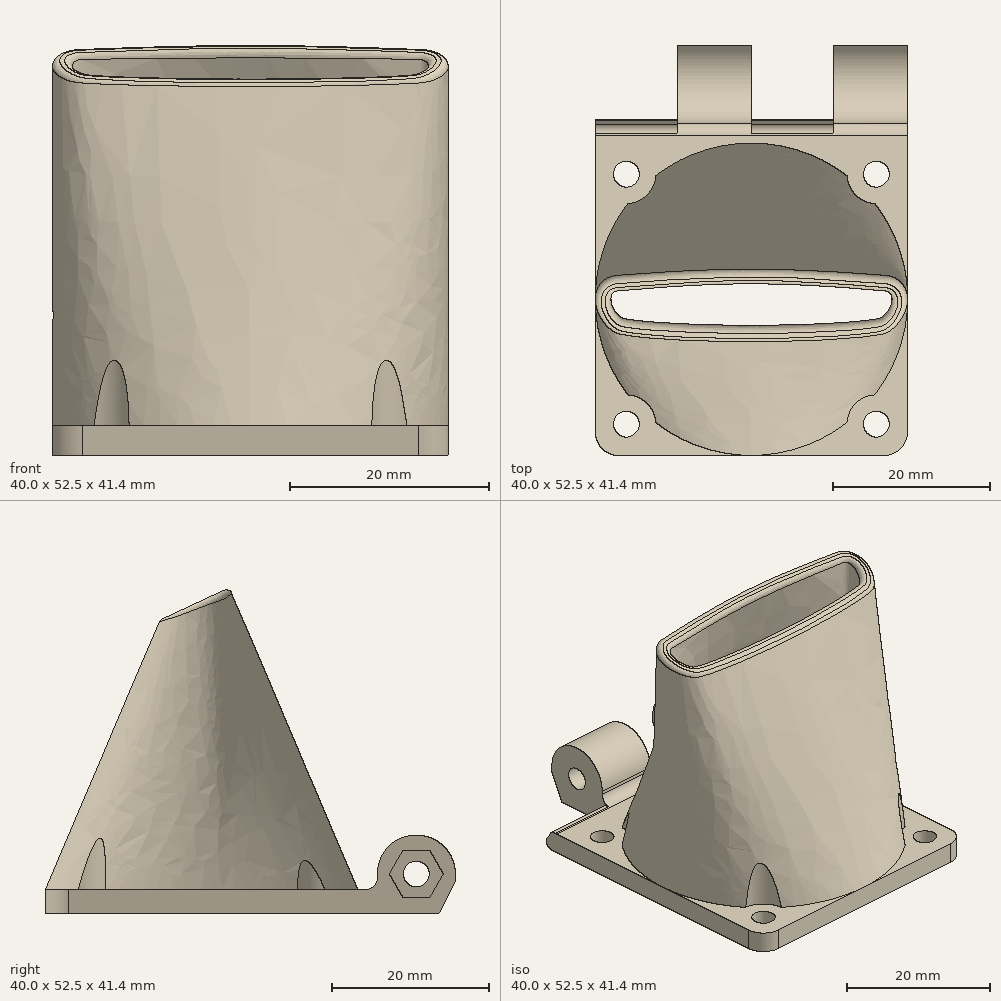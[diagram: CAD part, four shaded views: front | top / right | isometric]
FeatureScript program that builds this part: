
annotation { "Feature Type Name" : "Feature", "Feature Type Description" : "" }
export const myFeature = defineFeature(function(context is Context, id is Id, definition is map)
    precondition{}
    {
        {
            var Q0;
            Q0=qCreatedBy(makeId("Top.planeOp"),FACE);
            var sketch = newSketch(context, id + "F0", { "sketchPlane" : qUnion([Q0])});
            skLineSegment(sketch, "E0.bottom", {"start": v(0, 0) * mm, "end": v(40, 0) * mm, "construction": true});
            skLineSegment(sketch, "E0.top", {"start": v(3, -40) * mm, "end": v(37, -40) * mm});
            skLineSegment(sketch, "E0.left", {"start": v(0, 5) * mm, "end": v(0, -37) * mm});
            skLineSegment(sketch, "E0.right", {"start": v(40, 5) * mm, "end": v(40, -37) * mm});
            skLineSegment(sketch, "E1", {"start": v(0, 0) * mm, "end": v(40, -40) * mm, "construction": true});
            skLineSegment(sketch, "E2", {"start": v(0, -40) * mm, "end": v(40, 0) * mm, "construction": true});
            skLineSegment(sketch, "E3", {"start": v(20, 0) * mm, "end": v(20, -40) * mm, "construction": true});
            skCircle(sketch, "E4", {"center": v(20, -20) * mm, "radius": 18 * mm});
            skCircle(sketch, "E5", {"center": v(4, -4) * mm, "radius": 1.65 * mm});
            skCircle(sketch, "E6", {"center": v(36, -4) * mm, "radius": 1.65 * mm});
            skCircle(sketch, "E7", {"center": v(36, -36) * mm, "radius": 1.65 * mm});
            skCircle(sketch, "E8", {"center": v(4, -36) * mm, "radius": 1.65 * mm});
            skPoint(sketch, "E9.visualSharp", {"position": v(0, -40) * mm});
            skArc(sketch, "E9.filletArc", {"start": v(0, -37) * mm, "mid": v(0.88, -39.12) * mm, "end": v(3, -40) * mm});
            skPoint(sketch, "E10.visualSharp", {"position": v(40, -40) * mm});
            skArc(sketch, "E10.filletArc", {"start": v(37, -40) * mm, "mid": v(39.12, -39.12) * mm, "end": v(40, -37) * mm});
            skPoint(sketch, "E11.visualSharp", {"position": v(40, 0) * mm});
            skPoint(sketch, "E12.visualSharp", {"position": v(0, 0) * mm});
            skLineSegment(sketch, "E13", {"start": v(0, 5) * mm, "end": v(40, 5) * mm});
            skSolve(sketch);
        }
        {
            var Q0;
            Q0 = qSketchRegion(id + "F0", true);
            extrude(context, id + "F1", {"entities" : qUnion([Q0]), "depth" : 3 * mm});
        }
        {
            var Q0;
            Q0=makeQuery(id+"F1.opExtrude","CAP_FACE",FACE,{"disambiguationData":[OSD([sQuery(id+"F0.wireOp",EDGE,"E0.bottom"),sQuery(id+"F0.wireOp",EDGE,"E0.top"),sQuery(id+"F0.wireOp",EDGE,"E0.left"),sQuery(id+"F0.wireOp",EDGE,"E0.right"),sQuery(id+"F0.wireOp",EDGE,"E4"),sQuery(id+"F0.wireOp",EDGE,"E5"),sQuery(id+"F0.wireOp",EDGE,"E6"),sQuery(id+"F0.wireOp",EDGE,"E7"),sQuery(id+"F0.wireOp",EDGE,"E8"),sQuery(id+"F0.wireOp",EDGE,"E9.filletArc"),sQuery(id+"F0.wireOp",EDGE,"E10.filletArc"),sQuery(id+"F0.wireOp",EDGE,"E11.filletArc"),sQuery(id+"F0.wireOp",EDGE,"E12.filletArc")])],"isStart":false});
            var sketch = newSketch(context, id + "F2", { "sketchPlane" : qUnion([Q0])});
            skLineSegment(sketch, "E14", {"start": v(0, 0) * mm, "end": v(20, -20) * mm, "construction": true});
            skLineSegment(sketch, "E15", {"start": v(4, -36) * mm, "end": v(36, -4) * mm, "construction": true});
            skLineSegment(sketch, "E16", {"start": v(20, -20) * mm, "end": v(36, -36) * mm, "construction": true});
            skArc(sketch, "E17", {"start": v(5.86, -5.86) * mm, "mid": v(2.39, -10.53) * mm, "end": v(0.4, -16) * mm});
            skArc(sketch, "E18", {"start": v(5.86, -34.14) * mm, "mid": v(20, -40) * mm, "end": v(34.14, -34.14) * mm});
            skArc(sketch, "E19", {"start": v(34.14, -5.86) * mm, "mid": v(20, 0) * mm, "end": v(5.86, -5.86) * mm});
            skArc(sketch, "E20", {"start": v(34.14, -34.14) * mm, "mid": v(39.15, -25.76) * mm, "end": v(39.6, -16) * mm});
            skLineSegment(sketch, "E21", {"start": v(0, -16) * mm, "end": v(40, -16) * mm, "construction": true});
            skArc(sketch, "E22", {"start": v(0.4, -16) * mm, "mid": v(0.85, -25.76) * mm, "end": v(5.86, -34.14) * mm});
            skArc(sketch, "E23", {"start": v(39.6, -16) * mm, "mid": v(37.61, -10.53) * mm, "end": v(34.14, -5.86) * mm});
            skSolve(sketch);
        }
        {
            var Q0;
            Q0=makeQuery(id+"F2.imprint","IMPRINT",FACE,{"disambiguationData":[TD([[makeQuery(id+"F2.imprint","IMPRINT",EDGE,{"derivedFrom":makeQuery(id+"F1.opExtrude","CAP_EDGE",EDGE,{"disambiguationData":[OSD([sQuery(id+"F0.wireOp",EDGE,"E6")])],"isStart":false})}),-1.0]])]});
            cPlane(context, id + "F3", {"entities" : qUnion([Q0]), "cplaneType" : CPlaneType.OFFSET, "offset" : 40 * mm, "width" : 150 * mm, "height" : 150 * mm});
        }
        {
            var Q0;
            Q0=qCreatedBy(id+"F3.planeOp",FACE);
            var sketch = newSketch(context, id + "F4", { "sketchPlane" : qUnion([Q0])});
            skLineSegment(sketch, "E24", {"start": v(20, -20) * mm, "end": v(40, -20) * mm, "construction": true});
            skArc(sketch, "E25", {"start": v(3, -17) * mm, "mid": v(0.88, -17.88) * mm, "end": v(0, -20) * mm});
            skArc(sketch, "E26", {"start": v(37, -23) * mm, "mid": v(39.12, -22.12) * mm, "end": v(40, -20) * mm});
            skLineSegment(sketch, "E27", {"start": v(3, -17) * mm, "end": v(37, -17) * mm});
            skLineSegment(sketch, "E28", {"start": v(3, -23) * mm, "end": v(37, -23) * mm});
            skLineSegment(sketch, "E29", {"start": v(0, 0) * mm, "end": v(20, -20) * mm, "construction": true});
            skLineSegment(sketch, "E30", {"start": v(0, -20) * mm, "end": v(20, -20) * mm, "construction": true});
            skArc(sketch, "E31", {"start": v(0, -20) * mm, "mid": v(0.88, -22.12) * mm, "end": v(3, -23) * mm});
            skArc(sketch, "E32", {"start": v(40, -20) * mm, "mid": v(39.12, -17.88) * mm, "end": v(37, -17) * mm});
            skSolve(sketch);
        }
        {
            var Q0;
            Q0=makeQuery(id+"F1.opExtrude","SWEPT_FACE",FACE,{"disambiguationData":[OSD([sQuery(id+"F0.wireOp",EDGE,"E0.top")])]});
            cPlane(context, id + "F5", {"entities" : qUnion([Q0]), "cplaneType" : CPlaneType.OFFSET, "offset" : 20 * mm, "oppositeDirection" : true, "width" : 150 * mm, "height" : 150 * mm});
        }
        {
            var Q0;
            Q0=qCreatedBy(id+"F5.planeOp",FACE);
            var sketch = newSketch(context, id + "F6", { "sketchPlane" : qUnion([Q0])});
            skLineSegment(sketch, "E33", {"start": v(0, 0) * mm, "end": v(0, 3) * mm, "construction": true});
            skLineSegment(sketch, "E34", {"start": v(0, 3) * mm, "end": v(0, 43) * mm});
            skLineSegment(sketch, "E35", {"start": v(0, 0) * mm, "end": v(40, 0) * mm, "construction": true});
            skLineSegment(sketch, "E36", {"start": v(40, 0) * mm, "end": v(40, 3) * mm, "construction": true});
            skLineSegment(sketch, "E37", {"start": v(40, 3) * mm, "end": v(40, 43) * mm});
            skSolve(sketch);
        }
        {
            var Q0;
            Q0=makeQuery(id+"F1.opExtrude","SWEPT_FACE",FACE,{"disambiguationData":[OSD([sQuery(id+"F0.wireOp",EDGE,"E0.right")])]});
            cPlane(context, id + "F7", {"entities" : qUnion([Q0]), "cplaneType" : CPlaneType.OFFSET, "offset" : 20 * mm, "oppositeDirection" : true, "width" : 150 * mm, "height" : 150 * mm});
        }
        {
            var Q0;
            Q0=qCreatedBy(id+"F7.planeOp",FACE);
            var sketch = newSketch(context, id + "F8", { "sketchPlane" : qUnion([Q0])});
            skLineSegment(sketch, "E38", {"start": v(0, 0) * mm, "end": v(0, 3) * mm, "construction": true});
            skLineSegment(sketch, "E39", {"start": v(0, 3) * mm, "end": v(-40, 3) * mm, "construction": true});
            skLineSegment(sketch, "E40", {"start": v(0, 3) * mm, "end": v(0, 43) * mm, "construction": true});
            skLineSegment(sketch, "E41", {"start": v(0, 43) * mm, "end": v(-17, 43) * mm, "construction": true});
            skLineSegment(sketch, "E42", {"start": v(-17, 43) * mm, "end": v(-23, 43) * mm, "construction": true});
            skLineSegment(sketch, "E43", {"start": v(-23, 43) * mm, "end": v(-23, 46) * mm, "construction": true});
            skLineSegment(sketch, "E44", {"start": v(-40, 3) * mm, "end": v(-40, 0) * mm, "construction": true});
            skLineSegment(sketch, "E45", {"start": v(-23, 43) * mm, "end": v(-40, 3) * mm});
            skLineSegment(sketch, "E46", {"start": v(-17, 43) * mm, "end": v(0, 3) * mm});
            skSolve(sketch);
        }
        {
            var Q1;
            Q1 = qSketchRegion(id + "F4", true);
            var Q2;
            Q2 = qSketchRegion(id + "F2", true);
            var Q3;
            Q3=sQuery(id+"F6.wireOp",EDGE,"E34");
            var Q4;
            Q4=sQuery(id+"F6.wireOp",EDGE,"E37");
            var Q5;
            Q5=sQuery(id+"F8.wireOp",EDGE,"E46");
            var Q6;
            Q6=sQuery(id+"F8.wireOp",EDGE,"E45");
            loft(context, id + "F9", {"addGuides" : true, "sheetProfilesArray" : [{ "sheetProfileEntities" : qUnion([Q1]) }, { "sheetProfileEntities" : qUnion([Q2]) }], "guidesArray" : [{ "guideEntities" : qUnion([Q3]), "guideDerivativeType" : LoftGuideDerivativeType.DEFAULT, "guideDerivativeMagnitude" : 1 }, { "guideEntities" : qUnion([Q4]), "guideDerivativeType" : LoftGuideDerivativeType.DEFAULT, "guideDerivativeMagnitude" : 1 }, { "guideEntities" : qUnion([Q5]), "guideDerivativeType" : LoftGuideDerivativeType.DEFAULT, "guideDerivativeMagnitude" : 1 }, { "guideEntities" : qUnion([Q6]), "guideDerivativeType" : LoftGuideDerivativeType.DEFAULT, "guideDerivativeMagnitude" : 1 }]});
        }
        {
            var Q0;
            Q0=makeQuery(id+"F9.opLoft","CAP_FACE",FACE,{"disambiguationData":[OSD([makeQuery(id+"F4.imprint","IMPRINT",FACE,{"disambiguationData":[TD([[makeQuery(id+"F4.imprint","IMPRINT",EDGE,{"derivedFrom":sQuery(id+"F4.wireOp",EDGE,"E25")}),1.0]])]})])],"isStart":true});
            var Q1;
            {var subQ7=sQuery(id+"F2.wireOp",EDGE,"E17");Q1=makeQuery(id+"F9.opLoft","CAP_FACE",FACE,{"disambiguationData":[OSD([makeQuery(id+"F2.imprint","IMPRINT",FACE,{"disambiguationData":[TD([[makeQuery(id+"F2.imprint","IMPRINT",EDGE,{"derivedFrom":subQ7}),1.0]])]})])],"isStart":true});}
            shell(context, id + "F10", {"entities" : qUnion([Q0, Q1]), "thickness" : 2 * mm});
        }
        {
            var Q0;
            Q0=makeQuery(id+"F1.opExtrude","SWEPT_BODY",BODY,{"disambiguationData":[OSD([sQuery(id+"F0.wireOp",EDGE,"E0.bottom"),sQuery(id+"F0.wireOp",EDGE,"E0.top"),sQuery(id+"F0.wireOp",EDGE,"E0.left"),sQuery(id+"F0.wireOp",EDGE,"E0.right"),sQuery(id+"F0.wireOp",EDGE,"E4"),sQuery(id+"F0.wireOp",EDGE,"E5"),sQuery(id+"F0.wireOp",EDGE,"E6"),sQuery(id+"F0.wireOp",EDGE,"E7"),sQuery(id+"F0.wireOp",EDGE,"E8"),sQuery(id+"F0.wireOp",EDGE,"E9.filletArc"),sQuery(id+"F0.wireOp",EDGE,"E10.filletArc"),sQuery(id+"F0.wireOp",EDGE,"E11.filletArc"),sQuery(id+"F0.wireOp",EDGE,"E12.filletArc")])]});
            var Q1;
            Q1=makeQuery(id+"F9.opLoft","SWEPT_BODY",BODY,{"disambiguationData":[OSD([makeQuery(id+"F2.imprint","IMPRINT",FACE,{"disambiguationData":[TD([[makeQuery(id+"F2.imprint","IMPRINT",EDGE,{"derivedFrom":makeQuery(id+"F1.opExtrude","CAP_EDGE",EDGE,{"disambiguationData":[OSD([sQuery(id+"F0.wireOp",EDGE,"E4")])],"isStart":false})}),1.0]])]}),makeQuery(id+"F4.imprint","IMPRINT",FACE,{"disambiguationData":[TD([[makeQuery(id+"F4.imprint","IMPRINT",EDGE,{"derivedFrom":sQuery(id+"F4.wireOp",EDGE,"E25")}),1.0]])]}),sQuery(id+"F6.wireOp",EDGE,"E34"),sQuery(id+"F6.wireOp",EDGE,"E37")])]});
            booleanBodies(context, id + "F11", {"operationType" : BooleanOperationType.UNION, "tools" : qUnion([Q0, Q1])});
        }
        {
            var Q0;
            Q0=qCreatedBy(makeId("Right.planeOp"),FACE);
            var sketch = newSketch(context, id + "F12", { "sketchPlane" : qUnion([Q0])});
            skLineSegment(sketch, "E47", {"start": v(0, 0) * mm, "end": v(-20, 0) * mm, "construction": true});
            skLineSegment(sketch, "E48", {"start": v(-20, 0) * mm, "end": v(-20, 40) * mm, "construction": true});
            skLineSegment(sketch, "E49", {"start": v(-20, 40) * mm, "end": v(-1.87, 48.45) * mm});
            skLineSegment(sketch, "E50", {"start": v(-1.87, 48.45) * mm, "end": v(-6.95, 59.33) * mm});
            skLineSegment(sketch, "E51", {"start": v(-6.95, 59.33) * mm, "end": v(-43.2, 42.42) * mm});
            skLineSegment(sketch, "E52", {"start": v(-43.2, 42.42) * mm, "end": v(-38.13, 31.55) * mm});
            skLineSegment(sketch, "E53", {"start": v(-38.13, 31.55) * mm, "end": v(-20, 40) * mm});
            skSolve(sketch);
        }
        {
            var Q0;
            Q0 = qSketchRegion(id + "F12", true);
            extrude(context, id + "F13", {"entities" : qUnion([Q0]), "operationType" : NewBodyOperationType.REMOVE, "endBound" : BoundingType.THROUGH_ALL, "depth" : 25 * mm});
        }
        {
            var Q0;
            Q0=makeQuery(id+"F13.boolean.opBoolean","INTERSECT",EDGE,{"derivedFrom":[makeQuery(id+"F10.opShell","OFFSET_FACE",FACE,{"disambiguationData":[OSD([sQuery(id+"F2.wireOp",EDGE,"E17"),sQuery(id+"F2.wireOp",EDGE,"E18"),sQuery(id+"F2.wireOp",EDGE,"E22"),sQuery(id+"F4.wireOp",EDGE,"E31"),sQuery(id+"F6.wireOp",EDGE,"E34")])]}),makeQuery(id+"F13.opExtrude","SWEPT_FACE",FACE,{"disambiguationData":[OSD([sQuery(id+"F12.wireOp",EDGE,"E49"),sQuery(id+"F12.wireOp",EDGE,"E53")])]})]});
            var Q1;
            Q1=makeQuery(id+"F13.boolean.opBoolean","INTERSECT",EDGE,{"derivedFrom":[makeQuery(id+"F9.opLoft","SWEPT_FACE",FACE,{"disambiguationData":[OSD([sQuery(id+"F2.wireOp",EDGE,"E17"),sQuery(id+"F2.wireOp",EDGE,"E18"),sQuery(id+"F2.wireOp",EDGE,"E22"),sQuery(id+"F4.wireOp",EDGE,"E31"),sQuery(id+"F6.wireOp",EDGE,"E34")])]}),makeQuery(id+"F13.opExtrude","SWEPT_FACE",FACE,{"disambiguationData":[OSD([sQuery(id+"F12.wireOp",EDGE,"E49"),sQuery(id+"F12.wireOp",EDGE,"E53")])]})]});
            fillet(context, id + "F14", {"entities" : qUnion([Q0, Q1]), "radius" : 0.75 * mm, "tangentPropagation" : true, "allowEdgeOverflow" : false});
        }
        {
            var Q0;
            {var subQ0=sQuery(id+"F0.wireOp",EDGE,"E0.right");var subQ1=sQuery(id+"F0.wireOp",EDGE,"E10.filletArc");var subQ2=sQuery(id+"F0.wireOp",EDGE,"E7");var subQ3=sQuery(id+"F0.wireOp",EDGE,"E0.top");var subQ4=makeQuery(id+"F1.opExtrude","CAP_FACE",FACE,{"disambiguationData":[OSD([sQuery(id+"F0.wireOp",EDGE,"E0.bottom"),subQ3,sQuery(id+"F0.wireOp",EDGE,"E0.left"),subQ0,sQuery(id+"F0.wireOp",EDGE,"E4"),sQuery(id+"F0.wireOp",EDGE,"E5"),sQuery(id+"F0.wireOp",EDGE,"E6"),subQ2,sQuery(id+"F0.wireOp",EDGE,"E8"),sQuery(id+"F0.wireOp",EDGE,"E9.filletArc"),subQ1,sQuery(id+"F0.wireOp",EDGE,"E11.filletArc"),sQuery(id+"F0.wireOp",EDGE,"E12.filletArc")])],"isStart":false});Q0=makeQuery(id+"F11.opBoolean","SPLIT",FACE,{"disambiguationData":[TD([makeQuery(id+"F1.opExtrude","SWEPT_FACE",FACE,{"disambiguationData":[OSD([subQ2])]})])],"derivedFrom":subQ4});}
            var sketch = newSketch(context, id + "F15", { "sketchPlane" : qUnion([Q0])});
            skCircle(sketch, "E54", {"center": v(36, -36) * mm, "radius": 3.75 * mm});
            skLineSegment(sketch, "E55.bottom", {"start": v(36, -36) * mm, "end": v(4, -36) * mm, "construction": true});
            skLineSegment(sketch, "E55.top", {"start": v(36, -4) * mm, "end": v(4, -4) * mm, "construction": true});
            skLineSegment(sketch, "E55.left", {"start": v(36, -36) * mm, "end": v(36, -4) * mm, "construction": true});
            skLineSegment(sketch, "E55.right", {"start": v(4, -36) * mm, "end": v(4, -4) * mm, "construction": true});
            skCircle(sketch, "E56", {"center": v(4, -36) * mm, "radius": 3.75 * mm});
            skCircle(sketch, "E57", {"center": v(4, -4) * mm, "radius": 3.75 * mm});
            skCircle(sketch, "E58", {"center": v(36, -4) * mm, "radius": 3.75 * mm});
            skSolve(sketch);
        }
        {
            var Q0;
            Q0 = qSketchRegion(id + "F15", true);
            extrude(context, id + "F16", {"entities" : qUnion([Q0]), "operationType" : NewBodyOperationType.REMOVE, "depth" : 25 * mm});
        }
        {
            var Q0;
            Q0=qCreatedBy(makeId("Right.planeOp"),FACE);
            var sketch = newSketch(context, id + "F17", { "sketchPlane" : qUnion([Q0])});
            skLineSegment(sketch, "E59.bottom", {"start": v(2.5, 0) * mm, "end": v(10.5, 0) * mm});
            skLineSegment(sketch, "E59.top", {"start": v(2.5, 5) * mm, "end": v(12.5, 5) * mm, "construction": true});
            skLineSegment(sketch, "E59.left", {"start": v(2.5, 0) * mm, "end": v(2.5, 5) * mm});
            skLineSegment(sketch, "E59.right", {"start": v(12.5, 4) * mm, "end": v(12.5, 5) * mm});
            skArc(sketch, "E60", {"start": v(12.5, 5) * mm, "mid": v(7.5, 10) * mm, "end": v(2.5, 5) * mm});
            skLineSegment(sketch, "E61", {"start": v(7.5, 5) * mm, "end": v(7.5, 0) * mm, "construction": true});
            skCircle(sketch, "E62", {"center": v(7.5, 5) * mm, "radius": 1.65 * mm});
            skLineSegment(sketch, "E63", {"start": v(10.5, 0) * mm, "end": v(12.5, 4) * mm});
            skPoint(sketch, "E64.orphan", {"position": v(12.5, 0) * mm});
            skSolve(sketch);
        }
        {
            var Q0;
            Q0 = qSketchRegion(id + "F17", true);
            extrude(context, id + "F18", {"entities" : qUnion([Q0]), "operationType" : NewBodyOperationType.ADD, "depth" : 40 * mm});
        }
        {
            var Q0;
            Q0=makeQuery(id+"F18.boolean.opBoolean","MERGE",FACE,{"derivedFrom":[makeQuery(id+"F1.opExtrude","SWEPT_FACE",FACE,{"disambiguationData":[OSD([sQuery(id+"F0.wireOp",EDGE,"E0.right")])]}),makeQuery(id+"F18.opExtrude","CAP_FACE",FACE,{"disambiguationData":[OSD([sQuery(id+"F17.wireOp",EDGE,"E59.bottom"),sQuery(id+"F17.wireOp",EDGE,"E59.left"),sQuery(id+"F17.wireOp",EDGE,"E59.right"),sQuery(id+"F17.wireOp",EDGE,"E60"),sQuery(id+"F17.wireOp",EDGE,"E62"),sQuery(id+"F17.wireOp",EDGE,"E63")])],"isStart":false})]});
            cPlane(context, id + "F19", {"entities" : qUnion([Q0]), "cplaneType" : CPlaneType.OFFSET, "offset" : 9.5 * mm, "oppositeDirection" : true, "width" : 150 * mm, "height" : 150 * mm});
        }
        {
            var Q0;
            Q0=qCreatedBy(id+"F19.planeOp",FACE);
            var sketch = newSketch(context, id + "F20", { "sketchPlane" : qUnion([Q0])});
            skLineSegment(sketch, "E65", {"start": v(0, 0) * mm, "end": v(7.5, 0) * mm, "construction": true});
            skLineSegment(sketch, "E66", {"start": v(7.5, 0) * mm, "end": v(7.5, 5) * mm, "construction": true});
            skArc(sketch, "E67", {"start": v(13.25, 5) * mm, "mid": v(3.43, 9.07) * mm, "end": v(7.5, -0.75) * mm});
            skLineSegment(sketch, "E68", {"start": v(7.5, -0.75) * mm, "end": v(13.25, -0.75) * mm});
            skLineSegment(sketch, "E69", {"start": v(13.25, 5) * mm, "end": v(13.25, -0.75) * mm});
            skSolve(sketch);
        }
        {
            var Q0;
            Q0 = qSketchRegion(id + "F20", true);
            extrude(context, id + "F21", {"entities" : qUnion([Q0]), "operationType" : NewBodyOperationType.REMOVE, "oppositeDirection" : true, "depth" : 10.5 * mm});
        }
        {
            var Q0;
            Q0=makeQuery(id+"F18.boolean.opBoolean","MERGE",FACE,{"derivedFrom":[makeQuery(id+"F1.opExtrude","SWEPT_FACE",FACE,{"disambiguationData":[OSD([sQuery(id+"F0.wireOp",EDGE,"E0.right")])]}),makeQuery(id+"F18.opExtrude","CAP_FACE",FACE,{"disambiguationData":[OSD([sQuery(id+"F17.wireOp",EDGE,"E59.bottom"),sQuery(id+"F17.wireOp",EDGE,"E59.left"),sQuery(id+"F17.wireOp",EDGE,"E59.right"),sQuery(id+"F17.wireOp",EDGE,"E60"),sQuery(id+"F17.wireOp",EDGE,"E62"),sQuery(id+"F17.wireOp",EDGE,"E63")])],"isStart":false})]});
            cPlane(context, id + "F22", {"entities" : qUnion([Q0]), "cplaneType" : CPlaneType.OFFSET, "offset" : 29.5 * mm, "oppositeDirection" : true, "width" : 150 * mm, "height" : 150 * mm});
        }
        {
            var Q0;
            Q0=qCreatedBy(id+"F22.planeOp",FACE);
            var sketch = newSketch(context, id + "F23", { "sketchPlane" : qUnion([Q0])});
            skLineSegment(sketch, "E70", {"start": v(0, 0) * mm, "end": v(7.5, 0) * mm, "construction": true});
            skLineSegment(sketch, "E71", {"start": v(7.5, 0) * mm, "end": v(7.5, 5) * mm, "construction": true});
            skArc(sketch, "E72", {"start": v(13.25, 5) * mm, "mid": v(3.43, 9.07) * mm, "end": v(7.5, -0.75) * mm});
            skLineSegment(sketch, "E73", {"start": v(7.5, -0.75) * mm, "end": v(13.25, -0.75) * mm});
            skLineSegment(sketch, "E74", {"start": v(13.25, 5) * mm, "end": v(13.25, -0.75) * mm});
            skSolve(sketch);
        }
        {
            var Q0;
            Q0 = qSketchRegion(id + "F23", true);
            extrude(context, id + "F24", {"entities" : qUnion([Q0]), "operationType" : NewBodyOperationType.REMOVE, "endBound" : BoundingType.THROUGH_ALL, "oppositeDirection" : true, "depth" : 25 * mm});
        }
        {
            var Q0;
            {var subQ0=makeQuery(id+"F16.opExtrude","CAP_FACE",FACE,{"disambiguationData":[OSD([sQuery(id+"F15.wireOp",EDGE,"E58")])],"isStart":true});var subQ1=sQuery(id+"F0.wireOp",EDGE,"E13");var subQ2=sQuery(id+"F0.wireOp",EDGE,"E6");var subQ3=sQuery(id+"F0.wireOp",EDGE,"E5");var subQ4=sQuery(id+"F0.wireOp",EDGE,"E0.right");var subQ5=sQuery(id+"F0.wireOp",EDGE,"E0.left");var subQ6=makeQuery(id+"F1.opExtrude","CAP_FACE",FACE,{"disambiguationData":[OSD([sQuery(id+"F0.wireOp",EDGE,"E0.top"),subQ5,subQ4,sQuery(id+"F0.wireOp",EDGE,"E4"),subQ3,subQ2,sQuery(id+"F0.wireOp",EDGE,"E7"),sQuery(id+"F0.wireOp",EDGE,"E8"),sQuery(id+"F0.wireOp",EDGE,"E9.filletArc"),sQuery(id+"F0.wireOp",EDGE,"E10.filletArc"),subQ1])],"isStart":false});var subQ7=makeQuery(id+"F1.opExtrude","SWEPT_FACE",FACE,{"disambiguationData":[OSD([subQ4])]});var subQ8=makeQuery(id+"F16.opExtrude","CAP_FACE",FACE,{"disambiguationData":[OSD([sQuery(id+"F15.wireOp",EDGE,"E57")])],"isStart":true});var subQ9=sQuery(id+"F17.wireOp",EDGE,"E59.left");var subQ10=makeQuery(id+"F18.opExtrude","SWEPT_FACE",FACE,{"disambiguationData":[OSD([subQ9])]});Q0=makeQuery(id+"F21.boolean.opBoolean","SPLIT",EDGE,{"disambiguationData":[TD([subQ7])],"derivedFrom":makeQuery(id+"F18.boolean.opBoolean","INTERSECT",EDGE,{"derivedFrom":[makeQuery(id+"F16.boolean.opBoolean","MERGE",FACE,{"derivedFrom":[makeQuery(id+"F11.opBoolean","SPLIT",FACE,{"disambiguationData":[TD([makeQuery(id+"F1.opExtrude","SWEPT_FACE",FACE,{"disambiguationData":[OSD([subQ3])]})])],"derivedFrom":subQ6}),subQ8,subQ0]}),subQ10]})});}
            fillet(context, id + "F25", {"entities" : qUnion([Q0]), "radius" : 1.5 * mm, "allowEdgeOverflow" : false});
        }
        {
            var Q0;
            {var subQ0=makeQuery(id+"F16.opExtrude","CAP_FACE",FACE,{"disambiguationData":[OSD([sQuery(id+"F15.wireOp",EDGE,"E58")])],"isStart":true});var subQ1=sQuery(id+"F0.wireOp",EDGE,"E13");var subQ2=sQuery(id+"F0.wireOp",EDGE,"E6");var subQ3=sQuery(id+"F0.wireOp",EDGE,"E5");var subQ4=sQuery(id+"F0.wireOp",EDGE,"E0.right");var subQ5=sQuery(id+"F0.wireOp",EDGE,"E0.left");var subQ6=makeQuery(id+"F1.opExtrude","CAP_FACE",FACE,{"disambiguationData":[OSD([sQuery(id+"F0.wireOp",EDGE,"E0.top"),subQ5,subQ4,sQuery(id+"F0.wireOp",EDGE,"E4"),subQ3,subQ2,sQuery(id+"F0.wireOp",EDGE,"E7"),sQuery(id+"F0.wireOp",EDGE,"E8"),sQuery(id+"F0.wireOp",EDGE,"E9.filletArc"),sQuery(id+"F0.wireOp",EDGE,"E10.filletArc"),subQ1])],"isStart":false});var subQ7=makeQuery(id+"F1.opExtrude","SWEPT_FACE",FACE,{"disambiguationData":[OSD([subQ4])]});var subQ8=makeQuery(id+"F16.opExtrude","CAP_FACE",FACE,{"disambiguationData":[OSD([sQuery(id+"F15.wireOp",EDGE,"E57")])],"isStart":true});var subQ9=sQuery(id+"F17.wireOp",EDGE,"E59.left");var subQ10=makeQuery(id+"F18.opExtrude","SWEPT_FACE",FACE,{"disambiguationData":[OSD([subQ9])]});Q0=makeQuery(id+"F25.opFillet","BLEND_EDGE",EDGE,{"blendedFrom":[makeQuery(id+"F21.boolean.opBoolean","SPLIT",EDGE,{"disambiguationData":[TD([subQ7])],"derivedFrom":makeQuery(id+"F18.boolean.opBoolean","INTERSECT",EDGE,{"derivedFrom":[makeQuery(id+"F16.boolean.opBoolean","MERGE",FACE,{"derivedFrom":[makeQuery(id+"F11.opBoolean","SPLIT",FACE,{"disambiguationData":[TD([makeQuery(id+"F1.opExtrude","SWEPT_FACE",FACE,{"disambiguationData":[OSD([subQ3])]})])],"derivedFrom":subQ6}),subQ8,subQ0]}),subQ10]})}),makeQuery(id+"F24.boolean.opBoolean","COPY",FACE,{"derivedFrom":makeQuery(id+"F24.opExtrude","SWEPT_FACE",FACE,{"disambiguationData":[OSD([sQuery(id+"F23.wireOp",EDGE,"E72")])]})})],"blendedInto":[makeQuery(id+"F24.boolean.opBoolean","COPY",FACE,{"derivedFrom":makeQuery(id+"F24.opExtrude","SWEPT_FACE",FACE,{"disambiguationData":[OSD([sQuery(id+"F23.wireOp",EDGE,"E72")])]})})]});}
            var Q1;
            {var subQ0=sQuery(id+"F20.wireOp",EDGE,"E67");var subQ1=makeQuery(id+"F16.opExtrude","CAP_FACE",FACE,{"disambiguationData":[OSD([sQuery(id+"F15.wireOp",EDGE,"E58")])],"isStart":true});var subQ2=sQuery(id+"F0.wireOp",EDGE,"E13");var subQ3=sQuery(id+"F0.wireOp",EDGE,"E6");var subQ4=sQuery(id+"F0.wireOp",EDGE,"E5");var subQ5=sQuery(id+"F0.wireOp",EDGE,"E0.right");var subQ6=sQuery(id+"F0.wireOp",EDGE,"E0.left");var subQ7=makeQuery(id+"F1.opExtrude","CAP_FACE",FACE,{"disambiguationData":[OSD([sQuery(id+"F0.wireOp",EDGE,"E0.top"),subQ6,subQ5,sQuery(id+"F0.wireOp",EDGE,"E4"),subQ4,subQ3,sQuery(id+"F0.wireOp",EDGE,"E7"),sQuery(id+"F0.wireOp",EDGE,"E8"),sQuery(id+"F0.wireOp",EDGE,"E9.filletArc"),sQuery(id+"F0.wireOp",EDGE,"E10.filletArc"),subQ2])],"isStart":false});var subQ8=makeQuery(id+"F1.opExtrude","SWEPT_FACE",FACE,{"disambiguationData":[OSD([subQ5])]});var subQ9=makeQuery(id+"F16.opExtrude","CAP_FACE",FACE,{"disambiguationData":[OSD([sQuery(id+"F15.wireOp",EDGE,"E57")])],"isStart":true});var subQ10=sQuery(id+"F17.wireOp",EDGE,"E59.left");var subQ11=makeQuery(id+"F18.opExtrude","SWEPT_FACE",FACE,{"disambiguationData":[OSD([subQ10])]});Q1=makeQuery(id+"F25.opFillet","BLEND_EDGE",EDGE,{"blendedFrom":[makeQuery(id+"F21.boolean.opBoolean","SPLIT",EDGE,{"disambiguationData":[TD([subQ8])],"derivedFrom":makeQuery(id+"F18.boolean.opBoolean","INTERSECT",EDGE,{"derivedFrom":[makeQuery(id+"F16.boolean.opBoolean","MERGE",FACE,{"derivedFrom":[makeQuery(id+"F11.opBoolean","SPLIT",FACE,{"disambiguationData":[TD([makeQuery(id+"F1.opExtrude","SWEPT_FACE",FACE,{"disambiguationData":[OSD([subQ4])]})])],"derivedFrom":subQ7}),subQ9,subQ1]}),subQ11]})}),makeQuery(id+"F21.boolean.opBoolean","COPY",FACE,{"derivedFrom":makeQuery(id+"F21.opExtrude","SWEPT_FACE",FACE,{"disambiguationData":[OSD([subQ0])]})})],"blendedInto":[makeQuery(id+"F21.boolean.opBoolean","COPY",FACE,{"derivedFrom":makeQuery(id+"F21.opExtrude","SWEPT_FACE",FACE,{"disambiguationData":[OSD([subQ0])]})})]});}
            var Q2;
            Q2=makeQuery(id+"F24.boolean.opBoolean","INTERSECT",EDGE,{"derivedFrom":[makeQuery(id+"F18.boolean.opBoolean","MERGE",FACE,{"derivedFrom":[makeQuery(id+"F1.opExtrude","CAP_FACE",FACE,{"disambiguationData":[OSD([sQuery(id+"F0.wireOp",EDGE,"E0.top"),sQuery(id+"F0.wireOp",EDGE,"E0.left"),sQuery(id+"F0.wireOp",EDGE,"E0.right"),sQuery(id+"F0.wireOp",EDGE,"E4"),sQuery(id+"F0.wireOp",EDGE,"E5"),sQuery(id+"F0.wireOp",EDGE,"E6"),sQuery(id+"F0.wireOp",EDGE,"E7"),sQuery(id+"F0.wireOp",EDGE,"E8"),sQuery(id+"F0.wireOp",EDGE,"E9.filletArc"),sQuery(id+"F0.wireOp",EDGE,"E10.filletArc"),sQuery(id+"F0.wireOp",EDGE,"E13")])],"isStart":true}),makeQuery(id+"F18.opExtrude","SWEPT_FACE",FACE,{"disambiguationData":[OSD([sQuery(id+"F17.wireOp",EDGE,"E59.bottom")])]})]}),makeQuery(id+"F24.opExtrude","SWEPT_FACE",FACE,{"disambiguationData":[OSD([sQuery(id+"F23.wireOp",EDGE,"E72")])]})]});
            var Q3;
            Q3=makeQuery(id+"F21.boolean.opBoolean","INTERSECT",EDGE,{"derivedFrom":[makeQuery(id+"F18.boolean.opBoolean","MERGE",FACE,{"derivedFrom":[makeQuery(id+"F1.opExtrude","CAP_FACE",FACE,{"disambiguationData":[OSD([sQuery(id+"F0.wireOp",EDGE,"E0.top"),sQuery(id+"F0.wireOp",EDGE,"E0.left"),sQuery(id+"F0.wireOp",EDGE,"E0.right"),sQuery(id+"F0.wireOp",EDGE,"E4"),sQuery(id+"F0.wireOp",EDGE,"E5"),sQuery(id+"F0.wireOp",EDGE,"E6"),sQuery(id+"F0.wireOp",EDGE,"E7"),sQuery(id+"F0.wireOp",EDGE,"E8"),sQuery(id+"F0.wireOp",EDGE,"E9.filletArc"),sQuery(id+"F0.wireOp",EDGE,"E10.filletArc"),sQuery(id+"F0.wireOp",EDGE,"E13")])],"isStart":true}),makeQuery(id+"F18.opExtrude","SWEPT_FACE",FACE,{"disambiguationData":[OSD([sQuery(id+"F17.wireOp",EDGE,"E59.bottom")])]})]}),makeQuery(id+"F21.opExtrude","SWEPT_FACE",FACE,{"disambiguationData":[OSD([sQuery(id+"F20.wireOp",EDGE,"E67")])]})]});
            fillet(context, id + "F26", {"entities" : qUnion([Q0, Q1, Q2, Q3]), "radius" : 1 * mm, "tangentPropagation" : true, "allowEdgeOverflow" : false});
        }
        {
            var Q0;
            Q0=makeQuery(id+"F18.boolean.opBoolean","MERGE",FACE,{"derivedFrom":[makeQuery(id+"F1.opExtrude","SWEPT_FACE",FACE,{"disambiguationData":[OSD([sQuery(id+"F0.wireOp",EDGE,"E0.right")])]}),makeQuery(id+"F18.opExtrude","CAP_FACE",FACE,{"disambiguationData":[OSD([sQuery(id+"F17.wireOp",EDGE,"E59.bottom"),sQuery(id+"F17.wireOp",EDGE,"E59.left"),sQuery(id+"F17.wireOp",EDGE,"E59.right"),sQuery(id+"F17.wireOp",EDGE,"E60"),sQuery(id+"F17.wireOp",EDGE,"E62"),sQuery(id+"F17.wireOp",EDGE,"E63")])],"isStart":false})]});
            var sketch = newSketch(context, id + "F27", { "sketchPlane" : qUnion([Q0])});
            skCircle(sketch, "E75.cCircle", {"center": v(7.5, 5) * mm, "radius": 3 * mm, "construction": true});
            skLineSegment(sketch, "E75.0", {"start": v(5.77, 8) * mm, "end": v(9.23, 8) * mm});
            skLineSegment(sketch, "E75.1", {"start": v(9.23, 8) * mm, "end": v(10.96, 5) * mm});
            skLineSegment(sketch, "E75.2", {"start": v(10.96, 5) * mm, "end": v(9.23, 2) * mm});
            skLineSegment(sketch, "E75.3", {"start": v(9.23, 2) * mm, "end": v(5.77, 2) * mm});
            skLineSegment(sketch, "E75.4", {"start": v(5.77, 2) * mm, "end": v(4.04, 5) * mm});
            skLineSegment(sketch, "E75.5", {"start": v(4.04, 5) * mm, "end": v(5.77, 8) * mm});
            skPoint(sketch, "E75.0.midPoint", {"position": v(7.5, 8) * mm});
            skSolve(sketch);
        }
        {
            var Q0;
            Q0 = qSketchRegion(id + "F27", true);
            extrude(context, id + "F28", {"entities" : qUnion([Q0]), "operationType" : NewBodyOperationType.REMOVE, "oppositeDirection" : true, "depth" : 3 * mm});
        }
    });
